# Revit family: Sanitary_Taps-Mixers_hansgrohe_29231XXX-hansgrohe-Bidette-hand-shower-1_0001
name_source: partatom
category: Plumbing Fixtures
units: mm (PartAtom-declared; Revit-internal decimal feet)

## family parameters
Always vertical = No
Cut with Voids When Loaded = No
OmniClass Number = 23.31.11.00
OmniClass Title = Faucets
Part Type = Normal
Room Calculation Point = No
Round Connector Dimension = Use Diameter
Shared = No
Work Plane-Based = Yes

## types (6) — shared parameters
Default Elevation = 48"
Description = Hansgrohe Bidette hand shower 1jet E EcoSmart+ for cold water with shower holder and hose 125 cm
Manufacturer = Hansgrohe
Model = 29231XXX
Product Guid = 3e123a00-2de6-4217-9a97-21d5e12dcb1f
Product Page URL = https://www.hansgrohe.com
Product data url = https://bimobject.com
URL = https://www.hansgrohe.com
Version = 1

## type names (no varying parameters)
- 000 Chrome
- 140 Brushed Bronze
- 340 Brushed Black Chrome
- 670 Matte Black
- 700 Matt White
- 990 Polished Gold Optic

## geometry (parser evidence)
native form markers: Sweep x1
no freeform markers — native parametric forms only
